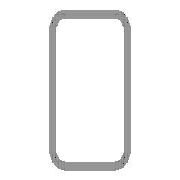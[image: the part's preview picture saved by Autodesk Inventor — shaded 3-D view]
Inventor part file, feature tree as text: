
AUTODESK INVENTOR PART (.ipt)
format: ipt  version: 2025 (Build 290162010, 162A)  size: 137,216 bytes
history: native  units: mm (DEFAULTED — no unit token found)
features: other x4, sketch x1, plane x1
ambient origin geometry x8: Origin, YZ Plane, XZ Plane, XY Plane, X Axis, Y Axis, Z Axis, Center Point
bodies: Solid1 (feature_tree), Body (feature_tree)
feature tree (6):
  parser-record x1  (decoder bookkeeping rows leaked as tree rows — omitted from the tree; the rows remain in map.json)
  other  "Driven Length"
  other  "Start Plane"
  other  "End Plane"
  sketch  "Sketch3"  dims[d3=920.0mm d4=0.0mm d7=3.75mm d10=60.0mm d11=40.0mm d12=2.5mm d13=40.0mm d14=960.0mm d15=30.0mm d16=20.0mm d17=90.0deg d18=920.0mm]
  plane  "Work Plane3"
